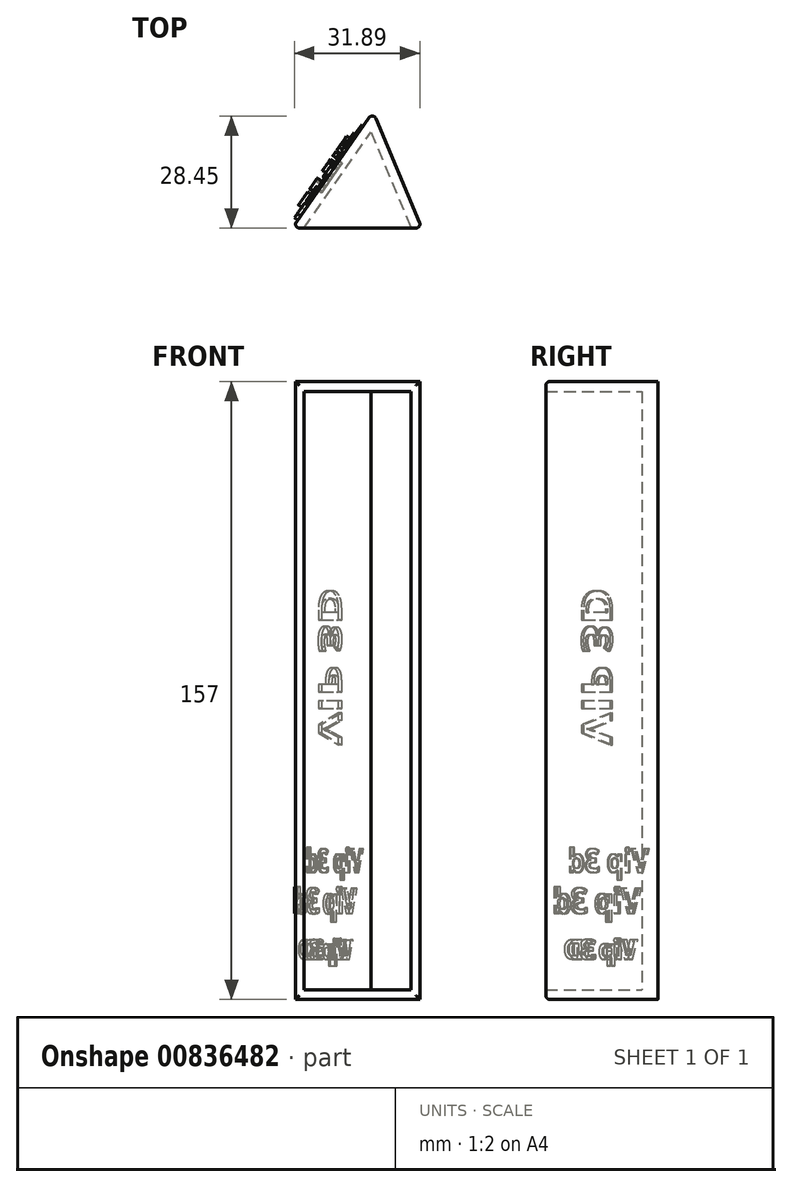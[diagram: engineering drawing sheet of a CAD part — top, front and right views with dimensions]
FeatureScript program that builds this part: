
annotation { "Feature Type Name" : "Feature", "Feature Type Description" : "" }
export const myFeature = defineFeature(function(context is Context, id is Id, definition is map)
    precondition{}
    {
        {
            var Q0;
            Q0=qCreatedBy(makeId("Top.planeOp"),FACE);
            var sketch = newSketch(context, id + "F0", { "sketchPlane" : qUnion([Q0])});
            skLineSegment(sketch, "E0", {"start": v(0, 0) * mm, "end": v(20.62, 29.5) * mm});
            skLineSegment(sketch, "E1", {"start": v(20.62, 29.5) * mm, "end": v(33, 0) * mm});
            skLineSegment(sketch, "E2", {"start": v(33, 0) * mm, "end": v(0, 0) * mm});
            skSolve(sketch);
        }
        {
            var Q0;
            Q0=makeQuery(id+"F0.imprint","IMPRINT",FACE,{"disambiguationData":[TD([[makeQuery(id+"F0.imprint","IMPRINT",EDGE,{"derivedFrom":sQuery(id+"F0.wireOp",EDGE,"E0")}),-1.0]])]});
            extrude(context, id + "F1", {"entities" : qUnion([Q0]), "endBound" : BoundingType.SYMMETRIC, "depth" : 157 * mm, "offsetDistance" : 25 * mm});
        }
        {
            var Q0;
            Q0=makeQuery(id+"F1.opExtrude","SWEPT_FACE",FACE,{"disambiguationData":[OSD([sQuery(id+"F0.wireOp",EDGE,"E2")])]});
            shell(context, id + "F2", {"entities" : qUnion([Q0]), "thickness" : 2.5 * mm});
        }
        {
            var Q0;
            Q0=makeQuery(id+"F1.opExtrude","SWEPT_EDGE",EDGE,{"disambiguationData":[OSD([sQuery(id+"F0.wireOp",EDGE,"E0"),sQuery(id+"F0.wireOp",EDGE,"E2")])]});
            var Q1;
            Q1=makeQuery(id+"F1.opExtrude","SWEPT_EDGE",EDGE,{"disambiguationData":[OSD([sQuery(id+"F0.wireOp",EDGE,"E0"),sQuery(id+"F0.wireOp",EDGE,"E1")])]});
            var Q2;
            Q2=makeQuery(id+"F1.opExtrude","CAP_EDGE",EDGE,{"disambiguationData":[OSD([sQuery(id+"F0.wireOp",EDGE,"E2")])],"isStart":true});
            var Q3;
            Q3=makeQuery(id+"F1.opExtrude","SWEPT_EDGE",EDGE,{"disambiguationData":[OSD([sQuery(id+"F0.wireOp",EDGE,"E1"),sQuery(id+"F0.wireOp",EDGE,"E2")])]});
            var Q4;
            Q4=makeQuery(id+"F1.opExtrude","CAP_EDGE",EDGE,{"disambiguationData":[OSD([sQuery(id+"F0.wireOp",EDGE,"E2")])],"isStart":false});
            fillet(context, id + "F3", {"entities" : qUnion([Q0, Q1, Q2, Q3, Q4]), "radius" : 1 * mm, "tangentPropagation" : true, "allowEdgeOverflow" : false});
        }
        {
            var Q0;
            Q0=makeQuery(id+"F1.opExtrude","SWEPT_FACE",FACE,{"disambiguationData":[OSD([sQuery(id+"F0.wireOp",EDGE,"E0")])]});
            var sketch = newSketch(context, id + "F4", { "sketchPlane" : qUnion([Q0])});
            skText(sketch, "E3", { "text": "VIP 3D", "fontName": "OpenSans-Bold.ttf"});
            const initialGuessF4  = {"E3": [-0.01169, -0.01387, 0, 1, 0.00904]};
            skSetInitialGuess(sketch, initialGuessF4);
            skSolve(sketch);
        }
        {
            var Q0;
            Q0 = qSketchRegion(id + "F4", true);
            extrude(context, id + "F5", {"entities" : qUnion([Q0]), "operationType" : NewBodyOperationType.REMOVE, "oppositeDirection" : true, "depth" : 1 * mm, "offsetDistance" : 25 * mm});
        }
        {
            var Q0;
            {var subQ2=sQuery(id+"F0.wireOp",EDGE,"E0");Q0=makeQuery(id+"F5.boolean.opBoolean","SPLIT",FACE,{"disambiguationData":[TD([makeQuery(id+"F5.opExtrude","SWEPT_FACE",FACE,{"disambiguationData":[OSD([sQuery(id+"F4.wireOp",EDGE,"E3.sketch_text.stroke-0")])]})])],"derivedFrom":makeQuery(id+"F1.opExtrude","SWEPT_FACE",FACE,{"disambiguationData":[OSD([subQ2])]})});}
            var sketch = newSketch(context, id + "F6", { "sketchPlane" : qUnion([Q0])});
            skText(sketch, "E4", { "text": "Vip 3D", "fontName": "OpenSans-Bold.ttf"});
            const initialGuessF6  = {"E4": [-0.02712, -0.06827, 1, 0, 0.00497]};
            skSetInitialGuess(sketch, initialGuessF6);
            skSolve(sketch);
        }
        {
            var Q0;
            Q0 = qSketchRegion(id + "F6", true);
            extrude(context, id + "F7", {"entities" : qUnion([Q0]), "operationType" : NewBodyOperationType.ADD, "depth" : 2 * mm, "offsetDistance" : 25 * mm});
        }
        {
            var Q0;
            {var subQ30=sQuery(id+"F0.wireOp",EDGE,"E0");var subQ51=makeQuery(id+"F5.opExtrude","SWEPT_FACE",FACE,{"disambiguationData":[OSD([sQuery(id+"F4.wireOp",EDGE,"E3.sketch_text.stroke-0")])]});Q0=makeQuery(id+"F7.boolean.opBoolean","SPLIT",FACE,{"disambiguationData":[TD([makeQuery(id+"F5.boolean.opBoolean","COPY",FACE,{"derivedFrom":subQ51})])],"derivedFrom":makeQuery(id+"F5.boolean.opBoolean","SPLIT",FACE,{"disambiguationData":[TD([subQ51])],"derivedFrom":makeQuery(id+"F1.opExtrude","SWEPT_FACE",FACE,{"disambiguationData":[OSD([subQ30])]})})});}
            var sketch = newSketch(context, id + "F8", { "sketchPlane" : qUnion([Q0])});
            skText(sketch, "E5", { "text": "Vip 3d", "fontName": "OpenSans-Bold.ttf"});
            const initialGuessF8  = {"E5": [-0.02892, -0.05661, 1, 0, 0.0064]};
            skSetInitialGuess(sketch, initialGuessF8);
            skSolve(sketch);
        }
        {
            var Q0;
            Q0 = qSketchRegion(id + "F8", true);
            extrude(context, id + "F9", {"entities" : qUnion([Q0]), "operationType" : NewBodyOperationType.ADD, "depth" : 1 * mm, "offsetDistance" : 25 * mm});
        }
        {
            var Q0;
            {var subQ123=makeQuery(id+"F5.opExtrude","SWEPT_FACE",FACE,{"disambiguationData":[OSD([sQuery(id+"F4.wireOp",EDGE,"E3.sketch_text.stroke-0")])]});var subQ124=makeQuery(id+"F5.boolean.opBoolean","COPY",FACE,{"derivedFrom":subQ123});var subQ140=sQuery(id+"F0.wireOp",EDGE,"E0");Q0=makeQuery(id+"F9.boolean.opBoolean","SPLIT",FACE,{"disambiguationData":[TD([subQ124])],"derivedFrom":makeQuery(id+"F7.boolean.opBoolean","SPLIT",FACE,{"disambiguationData":[TD([subQ124])],"derivedFrom":makeQuery(id+"F5.boolean.opBoolean","SPLIT",FACE,{"disambiguationData":[TD([subQ123])],"derivedFrom":makeQuery(id+"F1.opExtrude","SWEPT_FACE",FACE,{"disambiguationData":[OSD([subQ140])]})})})});}
            var sketch = newSketch(context, id + "F10", { "sketchPlane" : qUnion([Q0])});
            skText(sketch, "E6", { "text": "Vip 3d", "fontName": "OpenSans-Bold.ttf"});
            const initialGuessF10  = {"E6": [-0.03172, -0.04616, 1, 0, 0.00592]};
            skSetInitialGuess(sketch, initialGuessF10);
            skSolve(sketch);
        }
        {
            var Q0;
            Q0 = qSketchRegion(id + "F10", true);
            extrude(context, id + "F11", {"entities" : qUnion([Q0]), "operationType" : NewBodyOperationType.ADD, "depth" : .5 * mm, "offsetDistance" : 25 * mm});
        }
    });
